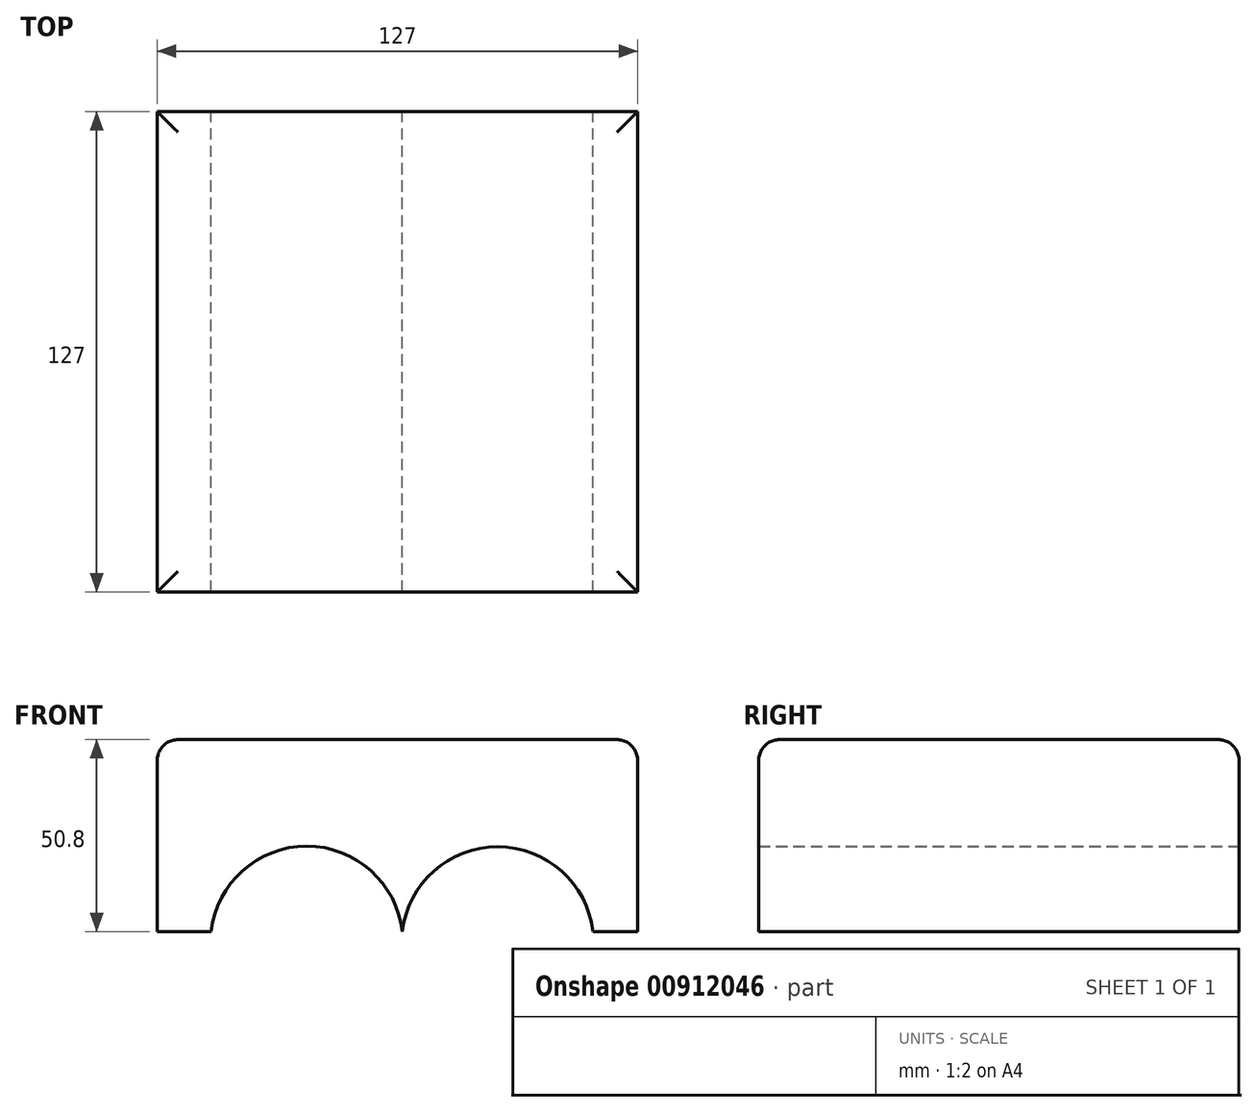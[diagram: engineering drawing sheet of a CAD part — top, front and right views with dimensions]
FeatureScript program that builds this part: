
annotation { "Feature Type Name" : "Feature", "Feature Type Description" : "" }
export const myFeature = defineFeature(function(context is Context, id is Id, definition is map)
    precondition{}
    {
        {
            var Q0;
            Q0=qCreatedBy(makeId("Front.planeOp"),FACE);
            var sketch = newSketch(context, id + "F0", { "sketchPlane" : qUnion([Q0])});
            skLineSegment(sketch, "E0.bottom", {"start": v(-64.76, 50.8) * mm, "end": v(62.24, 50.8) * mm});
            skLineSegment(sketch, "E0.top", {"start": v(-64.76, 0) * mm, "end": v(62.24, 0) * mm});
            skLineSegment(sketch, "E0.left", {"start": v(-64.76, 50.8) * mm, "end": v(-64.76, 0) * mm});
            skLineSegment(sketch, "E0.right", {"start": v(62.24, 50.8) * mm, "end": v(62.24, 0) * mm});
            skArc(sketch, "E1", {"start": v(0, 0) * mm, "mid": v(-25.25, 22.61) * mm, "end": v(-50.5, 0) * mm});
            skArc(sketch, "E2", {"start": v(50.46, 0) * mm, "mid": v(25.23, 22.46) * mm, "end": v(0, 0) * mm});
            skSolve(sketch);
        }
        {
            var Q0;
            Q0=makeQuery(id+"F0.imprint","IMPRINT",FACE,{"disambiguationData":[TD([[makeQuery(id+"F0.imprint","IMPRINT",EDGE,{"derivedFrom":sQuery(id+"F0.wireOp",EDGE,"E0.bottom")}),-1.0]])]});
            extrude(context, id + "F1", {"entities" : qUnion([Q0]), "depth" : 127 * mm, "offsetDistance" : 25.4 * mm});
        }
        {
            var Q0;
            Q0=makeQuery(id+"F1.opExtrude","CAP_EDGE",EDGE,{"disambiguationData":[OSD([sQuery(id+"F0.wireOp",EDGE,"E0.bottom")])],"isStart":true});
            var Q1;
            Q1=makeQuery(id+"F1.opExtrude","SWEPT_EDGE",EDGE,{"disambiguationData":[OSD([sQuery(id+"F0.wireOp",EDGE,"E0.bottom"),sQuery(id+"F0.wireOp",EDGE,"E0.left")])]});
            var Q2;
            Q2=makeQuery(id+"F1.opExtrude","CAP_EDGE",EDGE,{"disambiguationData":[OSD([sQuery(id+"F0.wireOp",EDGE,"E0.bottom")])],"isStart":false});
            var Q3;
            Q3=makeQuery(id+"F1.opExtrude","SWEPT_EDGE",EDGE,{"disambiguationData":[OSD([sQuery(id+"F0.wireOp",EDGE,"E0.bottom"),sQuery(id+"F0.wireOp",EDGE,"E0.right")])]});
            fillet(context, id + "F2", {"entities" : qUnion([Q0, Q1, Q2, Q3]), "radius" : 5.52 * mm, "tangentPropagation" : true, "allowEdgeOverflow" : false});
        }
    });
